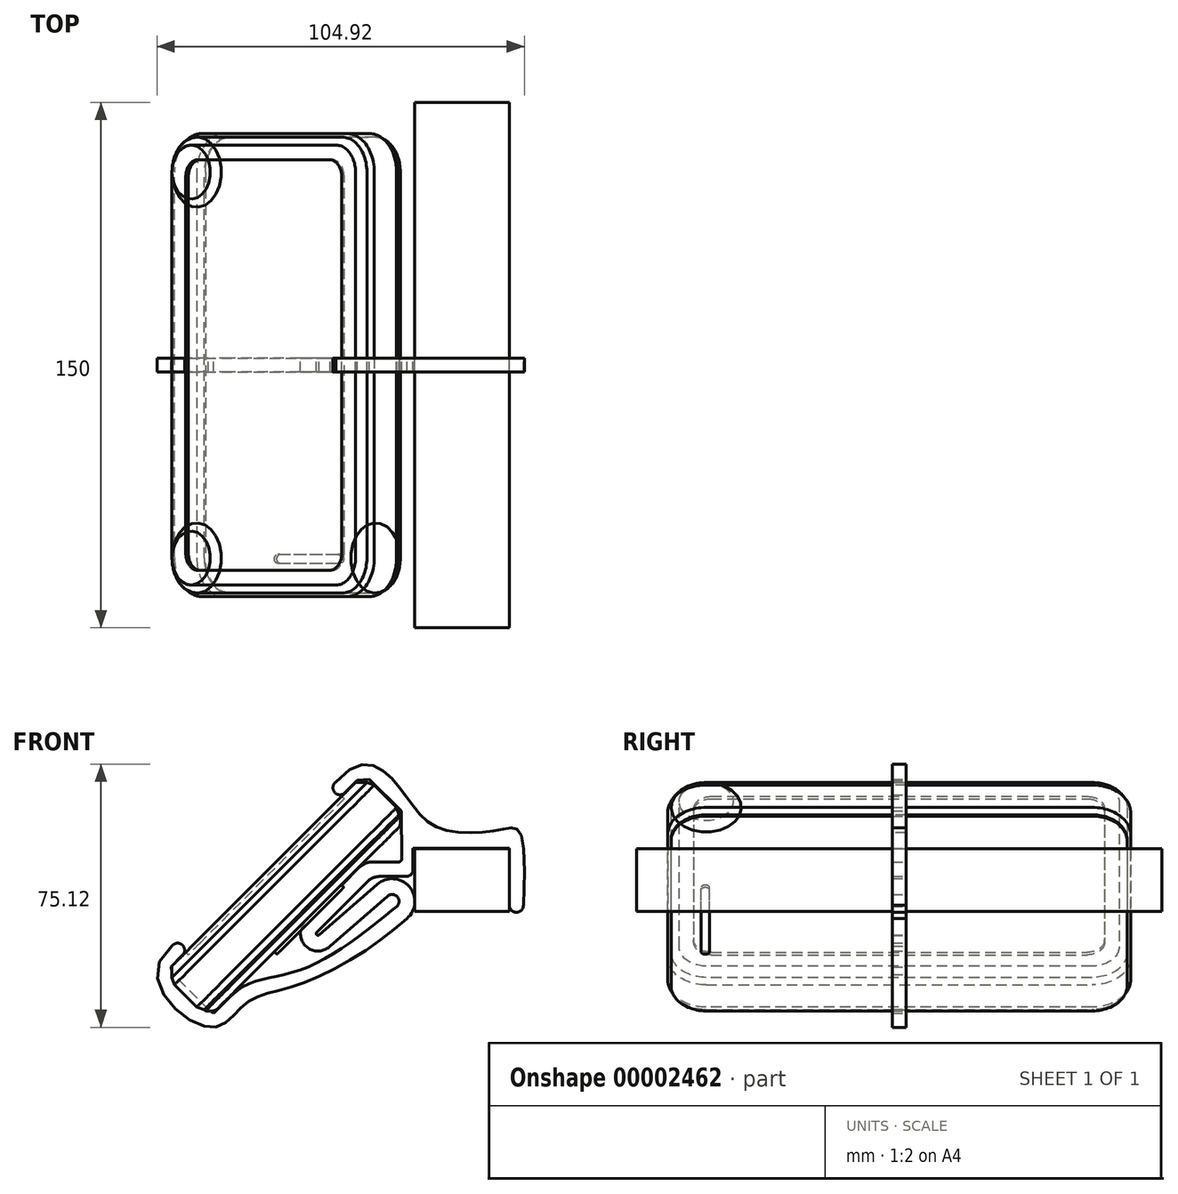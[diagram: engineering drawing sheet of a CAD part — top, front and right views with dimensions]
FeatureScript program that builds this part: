
annotation { "Feature Type Name" : "Feature", "Feature Type Description" : "" }
export const myFeature = defineFeature(function(context is Context, id is Id, definition is map)
    precondition{}
    {
        {
            var Q0;
            Q0=qCreatedBy(makeId("Right.planeOp"),FACE);
            var sketch = newSketch(context, id + "F0", { "sketchPlane" : qUnion([Q0])});
            skLineSegment(sketch, "E0", {"start": v(-84.74, 0) * mm, "end": v(84.74, 0) * mm, "construction": true});
            skSolve(sketch);
        }
        {
            var Q0;
            Q0=sQuery(id+"F0.wireOp",EDGE,"E0");
            cPlane(context, id + "F1", {"entities" : qUnion([Q0]), "cplaneType" : CPlaneType.LINE_ANGLE, "offset" : 150 * mm, "angle" : 315 * degree, "width" : 150 * mm, "height" : 150 * mm});
        }
        {
            var Q0;
            Q0=qCreatedBy(id+"F1.planeOp",FACE);
            var sketch = newSketch(context, id + "F2", { "sketchPlane" : qUnion([Q0])});
            skLineSegment(sketch, "E1.rect.bottom", {"start": v(55.1, -40.35) * mm, "end": v(-55.1, -40.35) * mm});
            skLineSegment(sketch, "E1.rect.top", {"start": v(55.1, 40.35) * mm, "end": v(-55.1, 40.35) * mm});
            skLineSegment(sketch, "E1.rect.left", {"start": v(66.1, -29.35) * mm, "end": v(66.1, 29.35) * mm});
            skLineSegment(sketch, "E1.rect.right", {"start": v(-66.1, -29.35) * mm, "end": v(-66.1, 29.35) * mm});
            skPoint(sketch, "E1.rect.middle", {"position": v(0, 0) * mm});
            skPoint(sketch, "E2.visualSharp", {"position": v(-66.1, 40.35) * mm});
            skArc(sketch, "E2.filletArc", {"start": v(-55.1, 40.35) * mm, "mid": v(-62.88, 37.13) * mm, "end": v(-66.1, 29.35) * mm});
            skPoint(sketch, "E3.visualSharp", {"position": v(66.1, 40.35) * mm});
            skArc(sketch, "E3.filletArc", {"start": v(66.1, 29.35) * mm, "mid": v(62.88, 37.13) * mm, "end": v(55.1, 40.35) * mm});
            skPoint(sketch, "E4.visualSharp", {"position": v(66.1, -40.35) * mm});
            skArc(sketch, "E4.filletArc", {"start": v(55.1, -40.35) * mm, "mid": v(62.88, -37.13) * mm, "end": v(66.1, -29.35) * mm});
            skPoint(sketch, "E5.visualSharp", {"position": v(-66.1, -40.35) * mm});
            skArc(sketch, "E5.filletArc", {"start": v(-66.1, -29.35) * mm, "mid": v(-62.88, -37.13) * mm, "end": v(-55.1, -40.35) * mm});
            skSolve(sketch);
        }
        {
            var Q0;
            Q0=qSketchRegion(id+"F2",true);
            extrude(context, id + "F3", {"entities" : qUnion([Q0]), "oppositeDirection" : true, "depth" : 13 * mm});
        }
        {
            var Q0;
            Q0=makeQuery(id+"F3.opExtrude","CAP_EDGE",EDGE,{"disambiguationData":[OSD([sQuery(id+"F2.wireOp",EDGE,"E1.rect.right")])],"isStart":false});
            var Q1;
            Q1=makeQuery(id+"F3.opExtrude","CAP_EDGE",EDGE,{"disambiguationData":[OSD([sQuery(id+"F2.wireOp",EDGE,"E1.rect.right")])],"isStart":true});
            chamfer(context, id + "F4", {"entities" : qUnion([Q0, Q1]), "chamferType" : ChamferType.TWO_OFFSETS, "width1" : 1 * mm, "oppositeDirection" : false, "width2" : 2 * mm, "tangentPropagation" : true});
        }
        {
            var Q0;
            Q0=makeQuery(id+"F3.opExtrude","CAP_FACE",FACE,{"disambiguationData":[OSD([sQuery(id+"F2.wireOp",EDGE,"E1.rect.bottom"),sQuery(id+"F2.wireOp",EDGE,"E1.rect.top"),sQuery(id+"F2.wireOp",EDGE,"E1.rect.left"),sQuery(id+"F2.wireOp",EDGE,"E1.rect.right"),sQuery(id+"F2.wireOp",EDGE,"E2.filletArc"),sQuery(id+"F2.wireOp",EDGE,"E3.filletArc"),sQuery(id+"F2.wireOp",EDGE,"E4.filletArc"),sQuery(id+"F2.wireOp",EDGE,"E5.filletArc")])],"isStart":false});
            var sketch = newSketch(context, id + "F5", { "sketchPlane" : qUnion([Q0])});
            skLineSegment(sketch, "E6.0", {"start": v(55.1, 39.35) * mm, "end": v(-55.1, 39.35) * mm});
            skLineSegment(sketch, "E6.2", {"start": v(65.1, -29.35) * mm, "end": v(65.1, 29.35) * mm});
            skLineSegment(sketch, "E6.4", {"start": v(-55.1, -39.35) * mm, "end": v(55.1, -39.35) * mm});
            skLineSegment(sketch, "E6.6", {"start": v(-65.1, 29.35) * mm, "end": v(-65.1, -29.35) * mm});
            skArc(sketch, "E7.0", {"start": v(-55.1, 39.35) * mm, "mid": v(-62.17, 36.42) * mm, "end": v(-65.1, 29.35) * mm});
            skArc(sketch, "E7.1", {"start": v(65.1, 29.35) * mm, "mid": v(62.17, 36.42) * mm, "end": v(55.1, 39.35) * mm});
            skArc(sketch, "E7.2", {"start": v(55.1, -39.35) * mm, "mid": v(62.17, -36.42) * mm, "end": v(65.1, -29.35) * mm});
            skArc(sketch, "E7.3", {"start": v(-65.1, -29.35) * mm, "mid": v(-62.17, -36.42) * mm, "end": v(-55.1, -39.35) * mm});
            skSolve(sketch);
        }
        {
            var Q0;
            Q0=qSketchRegion(id+"F5",true);
            extrude(context, id + "F6", {"entities" : qUnion([Q0]), "depth" : 2.5 * mm});
        }
        {
            var Q0;
            Q0=makeQuery(id+"F6.opExtrude","CAP_EDGE",EDGE,{"disambiguationData":[OSD([sQuery(id+"F5.wireOp",EDGE,"E6.2")])],"isStart":false});
            chamfer(context, id + "F7", {"entities" : qUnion([Q0]), "chamferType" : ChamferType.TWO_OFFSETS, "width1" : 2 * mm, "oppositeDirection" : false, "width2" : 2 * mm, "tangentPropagation" : true});
        }
        {
            var Q0;
            {var subQ0=sQuery(id+"F5.wireOp",EDGE,"E6.2");Q0=makeQuery(id+"F7.opChamfer","BLEND_EDGE",EDGE,{"blendedFrom":[makeQuery(id+"F6.opExtrude","CAP_EDGE",EDGE,{"disambiguationData":[OSD([subQ0])],"isStart":false}),makeQuery(id+"F6.opExtrude","CAP_FACE",FACE,{"disambiguationData":[OSD([sQuery(id+"F5.wireOp",EDGE,"E6.0"),sQuery(id+"F5.wireOp",EDGE,"E6.1"),subQ0,sQuery(id+"F5.wireOp",EDGE,"E6.3"),sQuery(id+"F5.wireOp",EDGE,"E6.4"),sQuery(id+"F5.wireOp",EDGE,"E6.5"),sQuery(id+"F5.wireOp",EDGE,"E6.6"),sQuery(id+"F5.wireOp",EDGE,"E6.7")])],"isStart":false})],"blendedInto":[makeQuery(id+"F6.opExtrude","CAP_FACE",FACE,{"disambiguationData":[OSD([sQuery(id+"F5.wireOp",EDGE,"E6.0"),sQuery(id+"F5.wireOp",EDGE,"E6.1"),subQ0,sQuery(id+"F5.wireOp",EDGE,"E6.3"),sQuery(id+"F5.wireOp",EDGE,"E6.4"),sQuery(id+"F5.wireOp",EDGE,"E6.5"),sQuery(id+"F5.wireOp",EDGE,"E6.6"),sQuery(id+"F5.wireOp",EDGE,"E6.7")])],"isStart":false})]});}
            fillet(context, id + "F8", {"entities" : qUnion([Q0]), "radius" : 2 * mm, "tangentPropagation" : true, "allowEdgeOverflow" : false});
        }
        {
            var Q0;
            Q0=makeQuery(id+"F3.opExtrude","CAP_FACE",FACE,{"disambiguationData":[OSD([sQuery(id+"F2.wireOp",EDGE,"E1.rect.bottom"),sQuery(id+"F2.wireOp",EDGE,"E1.rect.top"),sQuery(id+"F2.wireOp",EDGE,"E1.rect.left"),sQuery(id+"F2.wireOp",EDGE,"E1.rect.right"),sQuery(id+"F2.wireOp",EDGE,"E2.filletArc"),sQuery(id+"F2.wireOp",EDGE,"E3.filletArc"),sQuery(id+"F2.wireOp",EDGE,"E4.filletArc"),sQuery(id+"F2.wireOp",EDGE,"E5.filletArc")])],"isStart":true});
            var sketch = newSketch(context, id + "F9", { "sketchPlane" : qUnion([Q0])});
            skLineSegment(sketch, "E8.0", {"start": v(55.1, 39.35) * mm, "end": v(-55.1, 39.35) * mm});
            skLineSegment(sketch, "E8.2", {"start": v(65.1, -29.35) * mm, "end": v(65.1, 29.35) * mm});
            skLineSegment(sketch, "E8.4", {"start": v(-55.1, -39.35) * mm, "end": v(55.1, -39.35) * mm});
            skLineSegment(sketch, "E8.6", {"start": v(-65.1, 29.35) * mm, "end": v(-65.1, -29.35) * mm});
            skArc(sketch, "E9.0", {"start": v(-55.1, 39.35) * mm, "mid": v(-62.17, 36.42) * mm, "end": v(-65.1, 29.35) * mm});
            skArc(sketch, "E9.1", {"start": v(65.1, 29.35) * mm, "mid": v(62.17, 36.42) * mm, "end": v(55.1, 39.35) * mm});
            skArc(sketch, "E9.2", {"start": v(55.1, -39.35) * mm, "mid": v(62.17, -36.42) * mm, "end": v(65.1, -29.35) * mm});
            skArc(sketch, "E9.3", {"start": v(-65.1, -29.35) * mm, "mid": v(-62.17, -36.42) * mm, "end": v(-55.1, -39.35) * mm});
            skSolve(sketch);
        }
        {
            var Q0;
            Q0=qSketchRegion(id+"F9",true);
            extrude(context, id + "F10", {"entities" : qUnion([Q0]), "depth" : 2.3 * mm});
        }
        {
            var Q0;
            Q0=makeQuery(id+"F10.opExtrude","CAP_EDGE",EDGE,{"disambiguationData":[OSD([sQuery(id+"F9.wireOp",EDGE,"E8.2")])],"isStart":false});
            chamfer(context, id + "F11", {"entities" : qUnion([Q0]), "chamferType" : ChamferType.TWO_OFFSETS, "width1" : 2.3 * mm, "oppositeDirection" : false, "width2" : 2.3 * mm, "tangentPropagation" : true});
        }
        {
            var Q0;
            Q0=makeQuery(id+"F6.opExtrude","CAP_FACE",FACE,{"disambiguationData":[OSD([sQuery(id+"F5.wireOp",EDGE,"E6.0"),sQuery(id+"F5.wireOp",EDGE,"E6.1"),sQuery(id+"F5.wireOp",EDGE,"E6.2"),sQuery(id+"F5.wireOp",EDGE,"E6.3"),sQuery(id+"F5.wireOp",EDGE,"E6.4"),sQuery(id+"F5.wireOp",EDGE,"E6.5"),sQuery(id+"F5.wireOp",EDGE,"E6.6"),sQuery(id+"F5.wireOp",EDGE,"E6.7")])],"isStart":false});
            var sketch = newSketch(context, id + "F12", { "sketchPlane" : qUnion([Q0])});
            skLineSegment(sketch, "E10.rect.left", {"start": v(-54.1, -12.25) * mm, "end": v(-54.1, 12.25) * mm});
            skLineSegment(sketch, "E10.rect.right", {"start": v(-56.6, -12.25) * mm, "end": v(-56.6, 12.25) * mm});
            skPoint(sketch, "E10.rect.middle", {"position": v(-55.35, 0) * mm});
            skArc(sketch, "E11", {"start": v(-54.1, 12.25) * mm, "mid": v(-55.35, 13.5) * mm, "end": v(-56.6, 12.25) * mm});
            skArc(sketch, "E12", {"start": v(-56.6, -12.25) * mm, "mid": v(-55.35, -13.5) * mm, "end": v(-54.1, -12.25) * mm});
            skSolve(sketch);
        }
        {
            var Q0;
            Q0=qSketchRegion(id+"F12",true);
            extrude(context, id + "F13", {"entities" : qUnion([Q0]), "depth" : 1 * mm});
        }
        {
            var Q0;
            Q0=makeQuery(id+"F10.opExtrude","CAP_FACE",FACE,{"disambiguationData":[OSD([sQuery(id+"F9.wireOp",EDGE,"E8.0"),sQuery(id+"F9.wireOp",EDGE,"E8.1"),sQuery(id+"F9.wireOp",EDGE,"E8.2"),sQuery(id+"F9.wireOp",EDGE,"E8.3"),sQuery(id+"F9.wireOp",EDGE,"E8.4"),sQuery(id+"F9.wireOp",EDGE,"E8.5"),sQuery(id+"F9.wireOp",EDGE,"E8.6"),sQuery(id+"F9.wireOp",EDGE,"E8.7")])],"isStart":false});
            var sketch = newSketch(context, id + "F14", { "sketchPlane" : qUnion([Q0])});
            skLineSegment(sketch, "E13.rect.bottom", {"start": v(53.65, 31.5) * mm, "end": v(-53.65, 31.5) * mm});
            skLineSegment(sketch, "E13.rect.top", {"start": v(53.65, -31.5) * mm, "end": v(-53.65, -31.5) * mm});
            skLineSegment(sketch, "E13.rect.left", {"start": v(58.65, 26.5) * mm, "end": v(58.65, -26.5) * mm});
            skLineSegment(sketch, "E13.rect.right", {"start": v(-58.65, 26.5) * mm, "end": v(-58.65, -26.5) * mm});
            skPoint(sketch, "E13.rect.middle", {"position": v(0, 0) * mm});
            skPoint(sketch, "E14.visualSharp", {"position": v(-58.65, -31.5) * mm});
            skArc(sketch, "E14.filletArc", {"start": v(-58.65, -26.5) * mm, "mid": v(-57.19, -30.04) * mm, "end": v(-53.65, -31.5) * mm});
            skPoint(sketch, "E15.visualSharp", {"position": v(-58.65, 31.5) * mm});
            skArc(sketch, "E15.filletArc", {"start": v(-53.65, 31.5) * mm, "mid": v(-57.19, 30.04) * mm, "end": v(-58.65, 26.5) * mm});
            skPoint(sketch, "E16.visualSharp", {"position": v(58.65, 31.5) * mm});
            skArc(sketch, "E16.filletArc", {"start": v(58.65, 26.5) * mm, "mid": v(57.19, 30.04) * mm, "end": v(53.65, 31.5) * mm});
            skPoint(sketch, "E17.visualSharp", {"position": v(58.65, -31.5) * mm});
            skArc(sketch, "E17.filletArc", {"start": v(53.65, -31.5) * mm, "mid": v(57.19, -30.04) * mm, "end": v(58.65, -26.5) * mm});
            skSolve(sketch);
        }
        {
            var Q0;
            Q0=qSketchRegion(id+"F14",true);
            extrude(context, id + "F15", {"entities" : qUnion([Q0]), "operationType" : NewBodyOperationType.REMOVE, "oppositeDirection" : true, "depth" : 1 * mm});
        }
        {
            var Q0;
            Q0=qCreatedBy(makeId("Front.planeOp"),FACE);
            var sketch = newSketch(context, id + "F16", { "sketchPlane" : qUnion([Q0])});
            skLineSegment(sketch, "E18.rect.bottom", {"start": v(68.5, -9) * mm, "end": v(41.5, -9) * mm});
            skLineSegment(sketch, "E18.rect.top", {"start": v(68.5, 9) * mm, "end": v(41.5, 9) * mm});
            skLineSegment(sketch, "E18.rect.left", {"start": v(68.5, -9) * mm, "end": v(68.5, 9) * mm});
            skLineSegment(sketch, "E18.rect.right", {"start": v(41.5, -9) * mm, "end": v(41.5, 9) * mm});
            skPoint(sketch, "E18.rect.middle", {"position": v(55, 0) * mm});
            skLineSegment(sketch, "E19", {"start": v(21.53, 24.92) * mm, "end": v(25.05, 28.44) * mm});
            skLineSegment(sketch, "E20", {"start": v(25.05, 28.44) * mm, "end": v(28.55, 28.8) * mm});
            skLineSegment(sketch, "E21", {"start": v(28.55, 28.8) * mm, "end": v(37.59, 19.76) * mm});
            skLineSegment(sketch, "E22", {"start": v(37.59, 19.76) * mm, "end": v(37.8, 6.16) * mm});
            skLineSegment(sketch, "E23", {"start": v(-17.45, -36.93) * mm, "end": v(-15.94, -38) * mm});
            skLineSegment(sketch, "E24", {"start": v(-17.45, -36.93) * mm, "end": v(-27.44, -26.94) * mm});
            skLineSegment(sketch, "E25", {"start": v(-27.44, -26.94) * mm, "end": v(-28.17, -24.78) * mm});
            skLineSegment(sketch, "E26", {"start": v(-28.17, -24.78) * mm, "end": v(-24.82, -21.43) * mm});
            skLineSegment(sketch, "E27.2", {"start": v(68.5, -7.24) * mm, "end": v(68.5, 9.01) * mm});
            skLineSegment(sketch, "E27.3", {"start": v(68.5, 9.01) * mm, "end": v(41, 9.01) * mm});
            skArc(sketch, "E28", {"start": v(18.97, 27.98) * mm, "mid": v(18.58, 25.05) * mm, "end": v(21.53, 24.92) * mm});
            skFitSpline(sketch, "E29", {"points": [v(18.97, 27.98) * mm, v(36.17, 27.6) * mm, v(47.66, 15.2) * mm, v(65.88, 14.4) * mm, v(72.51, -7.24) * mm], "startDerivative": vector(93.81, 110.27) * mm, "endDerivative": vector(-12.06, -266.09) * mm});
            skArc(sketch, "E30", {"start": v(68.51, -7.24) * mm, "mid": v(70.51, -9.24) * mm, "end": v(72.51, -7.24) * mm});
            skArc(sketch, "E31", {"start": v(-24.82, -21.43) * mm, "mid": v(-24.96, -18.47) * mm, "end": v(-27.89, -18.89) * mm});
            skFitSpline(sketch, "E32", {"points": [v(-27.89, -18.89) * mm, v(-18, -41.93) * mm, v(-6.76, -35.24) * mm, v(8.31, -29.91) * mm, v(39.27, -11) * mm], "startDerivative": vector(-124.18, -96.69) * mm, "endDerivative": vector(77.38, 70.92) * mm});
            skArc(sketch, "E33", {"start": v(10.31, -11.75) * mm, "mid": v(10.31, -18.82) * mm, "end": v(17.38, -18.82) * mm});
            skLineSegment(sketch, "E34", {"start": v(10.31, -11.75) * mm, "end": v(17.38, -18.82) * mm, "construction": true});
            skArc(sketch, "E35", {"start": v(13.5, -14.93) * mm, "mid": v(13.5, -15.64) * mm, "end": v(14.2, -15.64) * mm});
            skLineSegment(sketch, "E36", {"start": v(13.5, -14.93) * mm, "end": v(27.97, -0.45) * mm});
            skLineSegment(sketch, "E37", {"start": v(41.5, -9) * mm, "end": v(68.5, 9) * mm, "construction": true});
            skLineSegment(sketch, "E38", {"start": v(14.2, -15.64) * mm, "end": v(30.74, -1.22) * mm});
            skLineSegment(sketch, "E39", {"start": v(17.38, -18.82) * mm, "end": v(33.69, -4.6) * mm});
            skArc(sketch, "E40", {"start": v(36.31, -7.62) * mm, "mid": v(36.5, -4.8) * mm, "end": v(33.69, -4.6) * mm});
            skArc(sketch, "E41", {"start": v(39.27, -11) * mm, "mid": v(39.9, -1.85) * mm, "end": v(30.74, -1.22) * mm});
            skLineSegment(sketch, "E42", {"start": v(39.27, -11) * mm, "end": v(30.74, -1.22) * mm, "construction": true});
            skFitSpline(sketch, "E43", {"points": [v(36.31, -7.62) * mm, v(9.98, -25.26) * mm, v(-11.24, -33.3) * mm], "startDerivative": vector(-30.56, -24.35) * mm, "endDerivative": vector(-38.63, -38.63) * mm});
            skLineSegment(sketch, "E44.trimOffspring", {"start": v(-11.24, -33.3) * mm, "end": v(-15.94, -38) * mm});
            skLineSegment(sketch, "E45", {"start": v(68.51, -7.24) * mm, "end": v(72.51, -7.24) * mm, "construction": true});
            skLineSegment(sketch, "E46.top", {"start": v(31.5, 1) * mm, "end": v(39, 1.01) * mm});
            skLineSegment(sketch, "E46.right", {"start": v(41, 9.01) * mm, "end": v(41, 3.01) * mm});
            skArc(sketch, "E47.filletArc", {"start": v(31.5, 1) * mm, "mid": v(29.6, 0.63) * mm, "end": v(27.97, -0.45) * mm});
            skPoint(sketch, "E48.visualSharp", {"position": v(41, 1.01) * mm});
            skArc(sketch, "E48.filletArc", {"start": v(39, 1.01) * mm, "mid": v(40.41, 1.6) * mm, "end": v(41, 3.01) * mm});
            skLineSegment(sketch, "E49.top", {"start": v(29.27, 5.14) * mm, "end": v(36.8, 5.14) * mm});
            skLineSegment(sketch, "E50.trimOffspring", {"start": v(25.74, 3.68) * mm, "end": v(10.31, -11.75) * mm});
            skArc(sketch, "E51.filletArc", {"start": v(36.8, 5.14) * mm, "mid": v(37.5, 5.44) * mm, "end": v(37.8, 6.16) * mm});
            skArc(sketch, "E52.filletArc", {"start": v(29.27, 5.14) * mm, "mid": v(27.36, 4.76) * mm, "end": v(25.74, 3.68) * mm});
            skSolve(sketch);
        }
        {
            var Q0;
            Q0=makeQuery(id+"F16.imprint","IMPRINT",FACE,{"disambiguationData":[TD([[makeQuery(id+"F16.imprint","IMPRINT",EDGE,{"derivedFrom":sQuery(id+"F16.wireOp",EDGE,"E19")}),1.0]])]});
            extrude(context, id + "F17", {"entities" : qUnion([Q0]), "endBound" : BoundingType.SYMMETRIC, "depth" : 4 * mm});
        }
        {
            var Q0;
            Q0=makeQuery(id+"F16.imprint","IMPRINT",FACE,{"disambiguationData":[TD([[makeQuery(id+"F16.imprint","IMPRINT",EDGE,{"derivedFrom":sQuery(id+"F16.wireOp",EDGE,"E18.rect.bottom")}),-1.0]])]});
            extrude(context, id + "F18", {"entities" : qUnion([Q0]), "endBound" : BoundingType.SYMMETRIC, "depth" : 150 * mm});
        }
    });
